# Revit family: Rohrschelle Sprinkler HDC, M10, Ø 20-116
name_source: partatom
category: HLS-Bauteile
revit_build: Autodesk Revit 2017 (Build: 20190507_1515(x64)
units: mm (PartAtom-declared; Revit-internal decimal feet)

## family parameters
Arbeitsebenenbasiert = Ja
Beim Laden mit Abzugskörper schneiden = Nein
Bemaßung runder Anschluss = Durchmesser verwenden
Gemeinsam genutzt = Ja
Immer vertikal = Nein
Raumberechnungspunkt = Nein
Teiletyp = Normal

## types (9) — shared parameters
A = 17 mm
Anschluss = M10
Bauart = zweiteilig
DVS = 5 mm  [stored 0.0164042 ft]
Fabrikat = Jiangmen Eurofix
Firma = MEFA Befestigungs- und Montagesysteme GmbH
H1 = 2 mm  [stored 0.00656168 ft]
HGA = 14 mm  [stored 0.0459318 ft]
MB = 30 mm  [stored 0.0984252 ft]
MD = 3 mm  [stored 0.00984252 ft]
Material = Stahl
Mengeneinheit = St
Oberflaeche = galvanisch verzinkt
Verschluss-Schraube = M10
Vorgabe-Ansicht = 1219 mm
max. zul. Last horizontal = 0.00 kN
max. zul. Last vertikal = 0.00 kN
zero-valued in all types: DS, Nennweite DN Rohr, Rohraußendurchmesser, Stärke Material

## per-type parameters (varying)
- RS Sprinkler HDC, M10, Ø 20- 24: AB=2 mm  [stored 0.00656168 ft]; Achsabstand=44 mm; Anschlußhöhe=17 mm; Artikelnummer=47300022; B=71 mm; Breite=66 mm; D=22 mm  [stored 0.0721785 ft]; D0=22 mm  [stored 0.0721785 ft]; DF1=22 mm  [stored 0.0721785 ft]; DF2=20 mm  [stored 0.0656168 ft]; Dmax=24 mm  [stored 0.0787402 ft]; Dmin=20 mm  [stored 0.0656168 ft]; EAN=4250928458209; Gewicht=0.14 kg; Gewicht pro Bauteil=0.14 kg; H=41 mm  [stored 0.134514 ft]; H2=5 mm  [stored 0.0164042 ft]; Höhe=44 mm; Kurztext1=Rohrschelle HDC 30x2,5; Kurztext2=20 - 24 mm M10; Materialmaße=30x2,5 mm; R=11 mm  [stored 0.0360892 ft]; RM=15 mm  [stored 0.0492126 ft]; Rohraußendurchmesser Zoll=1/2 Zoll; S=49 mm  [stored 0.160761 ft]; max. Rohraußendurchmesser=24 mm  [stored 0.0787402 ft]; max. zul. Last=2.50 kN; min. Rohraußendurchmesser=20 mm  [stored 0.0656168 ft]; vpe=50 St
- RS Sprinkler HDC, M10, Ø 25- 30: AB=1 mm  [stored 0.00328084 ft]; Achsabstand=50 mm; Anschlußhöhe=19 mm; Artikelnummer=47300027; B=76 mm; Breite=71 mm; D=26 mm; D0=26 mm; DF1=21 mm  [stored 0.0688976 ft]; DF2=20 mm  [stored 0.0656168 ft]; Dmax=30 mm  [stored 0.0984252 ft]; Dmin=25 mm  [stored 0.082021 ft]; EAN=4250928458216; Gewicht=0.15 kg; Gewicht pro Bauteil=0.15 kg; H=45 mm  [stored 0.147638 ft]; H2=5 mm  [stored 0.0164042 ft]; Höhe=52 mm; Kurztext1=Rohrschelle HDC 30x2,5; Kurztext2=25 - 30 mm M10; Materialmaße=30x2,5 mm; R=13 mm; RM=16 mm  [stored 0.0524934 ft]; Rohraußendurchmesser Zoll=3/4 Zoll; S=55 mm  [stored 0.180446 ft]; max. Rohraußendurchmesser=30 mm  [stored 0.0984252 ft]; max. zul. Last=2.50 kN; min. Rohraußendurchmesser=25 mm  [stored 0.082021 ft]; vpe=50 St
- RS Sprinkler HDC, M10, Ø 31- 35: AB=1 mm  [stored 0.00328084 ft]; Achsabstand=55 mm; Anschlußhöhe=18 mm; Artikelnummer=47300034; B=82 mm; Breite=77 mm; D=32 mm  [stored 0.104987 ft]; D0=32 mm  [stored 0.104987 ft]; DF1=22 mm  [stored 0.0721785 ft]; DF2=20 mm  [stored 0.0656168 ft]; Dmax=35 mm  [stored 0.114829 ft]; Dmin=31 mm  [stored 0.101706 ft]; EAN=4250928458223; Gewicht=0.16 kg; Gewicht pro Bauteil=0.16 kg; H=51 mm; H2=5 mm  [stored 0.0164042 ft]; Höhe=57 mm; Kurztext1=Rohrschelle HDC 30x2,5; Kurztext2=31 - 35 mm M10; Materialmaße=30x2,5 mm; R=16 mm  [stored 0.0524934 ft]; RM=19 mm; Rohraußendurchmesser Zoll=1 Zoll; S=60 mm  [stored 0.19685 ft]; max. Rohraußendurchmesser=35 mm  [stored 0.114829 ft]; max. zul. Last=2.50 kN; min. Rohraußendurchmesser=31 mm  [stored 0.101706 ft]; vpe=50 St
- RS Sprinkler HDC, M10, Ø 40- 45: AB=2 mm  [stored 0.00656168 ft]; Achsabstand=66 mm; Anschlußhöhe=18 mm; Artikelnummer=47300043; B=93 mm; Breite=88 mm; D=42 mm  [stored 0.137795 ft]; D0=42 mm  [stored 0.137795 ft]; DF1=22 mm  [stored 0.0721785 ft]; DF2=21 mm  [stored 0.0688976 ft]; Dmax=45 mm  [stored 0.147638 ft]; Dmin=40 mm  [stored 0.131234 ft]; EAN=4250928458230; Gewicht=0.17 kg; Gewicht pro Bauteil=0.17 kg; H=61 mm  [stored 0.200131 ft]; H2=5 mm  [stored 0.0164042 ft]; Höhe=67 mm; Kurztext1=Rohrschelle HDC 30x2,5; Kurztext2=40 - 45 mm M10; Materialmaße=30x2,5 mm; R=21 mm  [stored 0.0688976 ft]; RM=25 mm  [stored 0.082021 ft]; Rohraußendurchmesser Zoll=1 1/4 Zoll; S=71 mm; max. Rohraußendurchmesser=45 mm  [stored 0.147638 ft]; max. zul. Last=2.50 kN; min. Rohraußendurchmesser=40 mm  [stored 0.131234 ft]; vpe=50 St
- RS Sprinkler HDC, M10, Ø 48- 53: AB=2 mm  [stored 0.00656168 ft]; Achsabstand=74 mm; Anschlußhöhe=18 mm; Artikelnummer=47300050; B=101 mm; Breite=96 mm; D=50 mm  [stored 0.164042 ft]; D0=50 mm  [stored 0.164042 ft]; DF1=22 mm  [stored 0.0721785 ft]; DF2=21 mm  [stored 0.0688976 ft]; Dmax=53 mm  [stored 0.173885 ft]; Dmin=48 mm  [stored 0.15748 ft]; EAN=4250928458247; Gewicht=0.19 kg; Gewicht pro Bauteil=0.19 kg; H=69 mm; H2=5 mm  [stored 0.0164042 ft]; Höhe=75 mm; Kurztext1=Rohrschelle HDC 30x2,5; Kurztext2=48 - 53 mm M10; Materialmaße=30x2,5 mm; R=25 mm  [stored 0.082021 ft]; RM=29 mm; Rohraußendurchmesser Zoll=1 1/2 Zoll; S=79 mm; max. Rohraußendurchmesser=53 mm  [stored 0.173885 ft]; max. zul. Last=2.50 kN; min. Rohraußendurchmesser=48 mm  [stored 0.15748 ft]; vpe=50 St
- RS Sprinkler HDC, M10, Ø 60- 65: AB=2 mm  [stored 0.00656168 ft]; Achsabstand=87 mm; Anschlußhöhe=18 mm; Artikelnummer=47300060; B=113 mm; Breite=108 mm; D=62 mm; D0=62 mm; DF1=21 mm  [stored 0.0688976 ft]; DF2=22 mm  [stored 0.0721785 ft]; Dmax=65 mm; Dmin=60 mm  [stored 0.19685 ft]; EAN=4250928458254; Gewicht=0.22 kg; Gewicht pro Bauteil=0.22 kg; H=81 mm; H2=5 mm  [stored 0.0164042 ft]; Höhe=87 mm; Kurztext1=Rohrschelle HDC 30x2,5; Kurztext2=60 - 65 mm M10; Materialmaße=30x2,5 mm; R=31 mm  [stored 0.101706 ft]; RM=35 mm  [stored 0.114829 ft]; Rohraußendurchmesser Zoll=2 Zoll; S=92 mm; max. Rohraußendurchmesser=65 mm; max. zul. Last=2.50 kN; min. Rohraußendurchmesser=60 mm  [stored 0.19685 ft]; vpe=25 St
- RS Sprinkler HDC, M10, Ø 76- 81: AB=2 mm  [stored 0.00656168 ft]; Achsabstand=108 mm; Anschlußhöhe=20 mm; Artikelnummer=47300076; B=135 mm; Breite=135 mm; D=78 mm; D0=78 mm; DF1=27 mm  [stored 0.0885827 ft]; DF2=21 mm  [stored 0.0688976 ft]; Dmax=81 mm; Dmin=76 mm; EAN=4250928458261; Gewicht=0.29 kg; Gewicht pro Bauteil=0.29 kg; H=98 mm; H2=6 mm  [stored 0.019685 ft]; Höhe=105 mm; Kurztext1=Rohrschelle HDC 30x3; Kurztext2=76 - 81 mm M10; Materialmaße=30x3 mm; R=39 mm  [stored 0.127953 ft]; RM=43 mm  [stored 0.141076 ft]; Rohraußendurchmesser Zoll=2 1/2 Zoll; S=108 mm; max. Rohraußendurchmesser=81 mm; max. zul. Last=3.50 kN; min. Rohraußendurchmesser=76 mm; vpe=25 St
- RS Sprinkler HDC, M10, Ø 88- 93: AB=2 mm  [stored 0.00656168 ft]; Achsabstand=120 mm; Anschlußhöhe=20 mm; Artikelnummer=47300088; B=147 mm; Breite=147 mm; D=90 mm; D0=90 mm; DF1=27 mm  [stored 0.0885827 ft]; DF2=21 mm  [stored 0.0688976 ft]; Dmax=93 mm; Dmin=88 mm; EAN=4250928458278; Gewicht=0.32 kg; Gewicht pro Bauteil=0.32 kg; H=110 mm; H2=6 mm  [stored 0.019685 ft]; Höhe=117 mm; Kurztext1=Rohrschelle HDC 30x3; Kurztext2=88 - 93 mm M10; Materialmaße=30x3 mm; R=45 mm  [stored 0.147638 ft]; RM=49 mm  [stored 0.160761 ft]; Rohraußendurchmesser Zoll=3 Zoll; S=120 mm; max. Rohraußendurchmesser=93 mm; max. zul. Last=3.50 kN; min. Rohraußendurchmesser=88 mm; vpe=25 St
- RS Sprinkler HDC, M10, Ø110-116: AB=2 mm  [stored 0.00656168 ft]; Achsabstand=144 mm; Anschlußhöhe=20 mm; Artikelnummer=47300110; B=171 mm; Breite=171 mm; D=112 mm; D0=112 mm; DF1=27 mm  [stored 0.0885827 ft]; DF2=22 mm  [stored 0.0721785 ft]; Dmax=116 mm; Dmin=110 mm; EAN=4250928458285; Gewicht=0.37 kg; Gewicht pro Bauteil=0.37 kg; H=132 mm; H2=6 mm  [stored 0.019685 ft]; Höhe=140 mm; Kurztext1=Rohrschelle HDC 30x3; Kurztext2=110 - 116 mm M10; Materialmaße=30x3 mm; R=56 mm  [stored 0.183727 ft]; RM=60 mm  [stored 0.19685 ft]; Rohraußendurchmesser Zoll=4 Zoll; S=144 mm; max. Rohraußendurchmesser=116 mm; max. zul. Last=3.50 kN; min. Rohraußendurchmesser=110 mm; vpe=25 St

note: [stored X ft] marks values corroborated as IEEE doubles in the binary element streams (Revit-internal decimal feet)

## geometry (parser evidence)
native form markers: Sweep x3
no freeform markers — native parametric forms only
